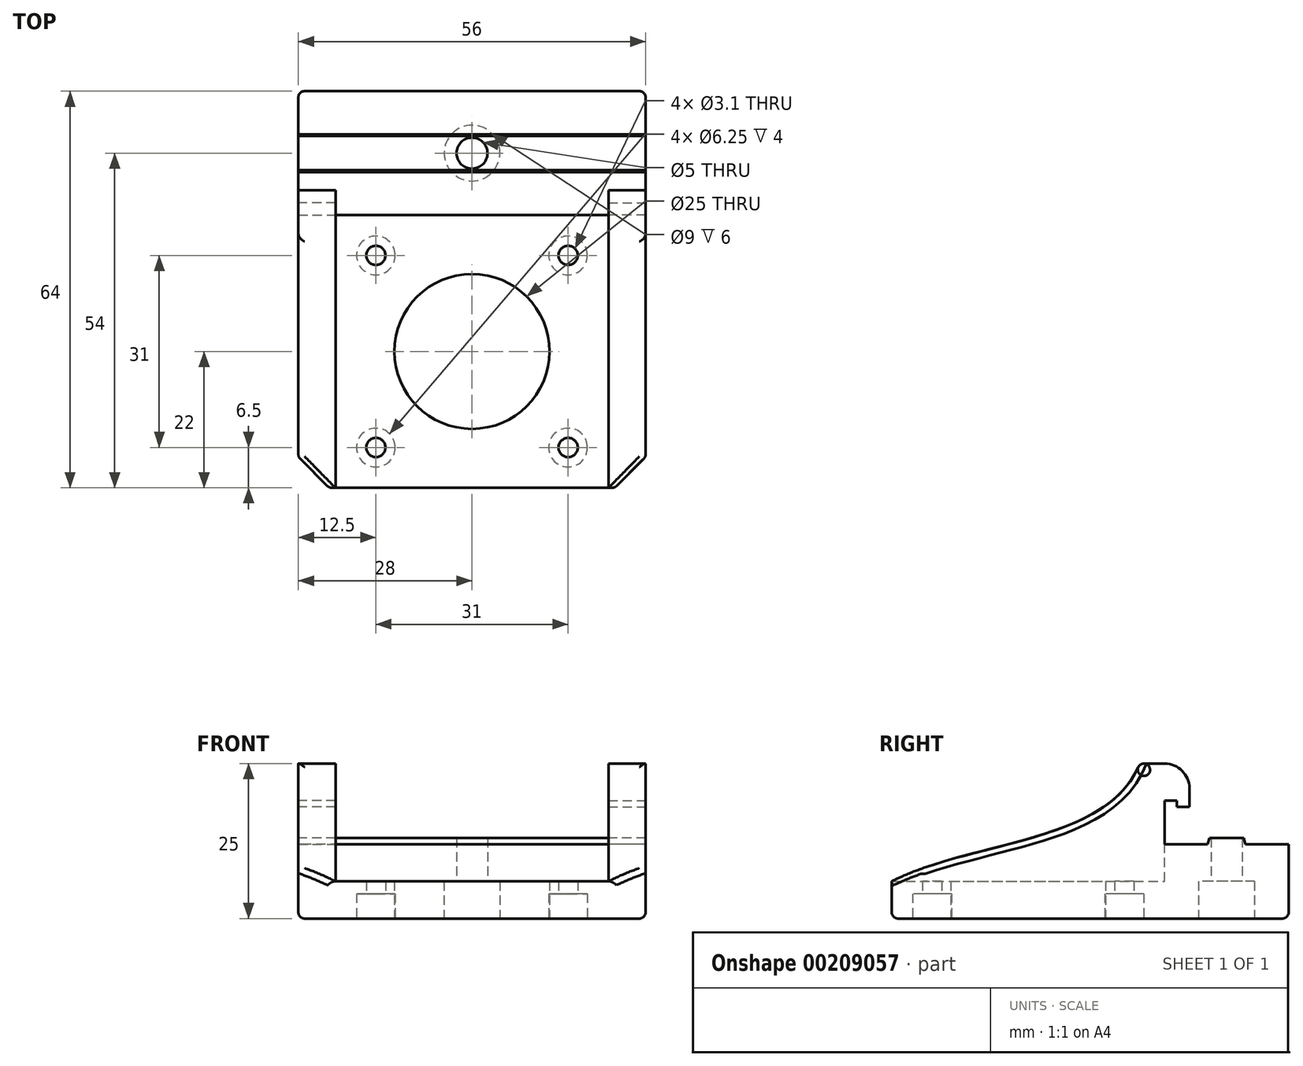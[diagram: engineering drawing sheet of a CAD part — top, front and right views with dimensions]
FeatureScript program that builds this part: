
annotation { "Feature Type Name" : "Feature", "Feature Type Description" : "" }
export const myFeature = defineFeature(function(context is Context, id is Id, definition is map)
    precondition{}
    {
        {
            var Q0;
            Q0=qCreatedBy(makeId("Right.planeOp"),FACE);
            var sketch = newSketch(context, id + "F0", { "sketchPlane" : qUnion([Q0])});
            skLineSegment(sketch, "E0", {"start": v(-6, 44) * mm, "end": v(0, 44) * mm});
            skLineSegment(sketch, "E1", {"start": v(0, 44) * mm, "end": v(0, 0) * mm});
            skLineSegment(sketch, "E2", {"start": v(0, 0) * mm, "end": v(6, 0) * mm});
            skLineSegment(sketch, "E3", {"start": v(6, 0) * mm, "end": v(6, -6.95) * mm});
            skLineSegment(sketch, "E4", {"start": v(7, -7.25) * mm, "end": v(7, -12.75) * mm});
            skLineSegment(sketch, "E5", {"start": v(7, -12.75) * mm, "end": v(6, -13.05) * mm});
            skLineSegment(sketch, "E6", {"start": v(6, -13.05) * mm, "end": v(6, -20) * mm});
            skLineSegment(sketch, "E7", {"start": v(6, -20) * mm, "end": v(-6, -20) * mm});
            skLineSegment(sketch, "E8", {"start": v(-6, -20) * mm, "end": v(-6, 44) * mm});
            skLineSegment(sketch, "E9", {"start": v(7, -7.25) * mm, "end": v(6, -6.95) * mm});
            skSolve(sketch);
        }
        {
            var Q0;
            Q0=makeQuery(id+"F0.imprint","IMPRINT",FACE,{"disambiguationData":[TD([[makeQuery(id+"F0.imprint","IMPRINT",EDGE,{"derivedFrom":sQuery(id+"F0.wireOp",EDGE,"E0")}),-1.0]])]});
            extrude(context, id + "F1", {"entities" : qUnion([Q0]), "endBound" : BoundingType.SYMMETRIC, "depth" : 56 * mm});
        }
        {
            var Q0;
            Q0=makeQuery(id+"F1.opExtrude","SWEPT_FACE",FACE,{"disambiguationData":[OSD([sQuery(id+"F0.wireOp",EDGE,"E8")])]});
            var sketch = newSketch(context, id + "F2", { "sketchPlane" : qUnion([Q0])});
            skLineSegment(sketch, "E10", {"start": v(-28, 44) * mm, "end": v(28, 0) * mm, "construction": true});
            skLineSegment(sketch, "E11", {"start": v(-28, 0) * mm, "end": v(28, 44) * mm, "construction": true});
            skLineSegment(sketch, "E12", {"start": v(-28, 0) * mm, "end": v(28, -20) * mm, "construction": true});
            skLineSegment(sketch, "E13", {"start": v(28, 0) * mm, "end": v(-28, -20) * mm, "construction": true});
            skLineSegment(sketch, "E14.bottom", {"start": v(-15.5, 37.5) * mm, "end": v(15.5, 37.5) * mm, "construction": true});
            skLineSegment(sketch, "E14.top", {"start": v(-15.5, 6.5) * mm, "end": v(15.5, 6.5) * mm, "construction": true});
            skLineSegment(sketch, "E14.left", {"start": v(-15.5, 37.5) * mm, "end": v(-15.5, 6.5) * mm, "construction": true});
            skLineSegment(sketch, "E14.right", {"start": v(15.5, 37.5) * mm, "end": v(15.5, 6.5) * mm, "construction": true});
            skLineSegment(sketch, "E15", {"start": v(-15.5, 37.5) * mm, "end": v(15.5, 6.5) * mm, "construction": true});
            skLineSegment(sketch, "E16", {"start": v(15.5, 37.5) * mm, "end": v(-15.5, 6.5) * mm, "construction": true});
            skPoint(sketch, "E17", {"position": v(0, 22) * mm});
            skCircle(sketch, "E18", {"center": v(-15.5, 37.5) * mm, "radius": 1.55 * mm});
            skCircle(sketch, "E19", {"center": v(15.5, 37.5) * mm, "radius": 1.55 * mm});
            skCircle(sketch, "E20", {"center": v(15.5, 6.5) * mm, "radius": 1.55 * mm});
            skCircle(sketch, "E21", {"center": v(-15.5, 6.5) * mm, "radius": 1.55 * mm});
            skPoint(sketch, "E22", {"position": v(0, -10) * mm});
            skCircle(sketch, "E23", {"center": v(0, -10) * mm, "radius": 2.5 * mm});
            skCircle(sketch, "E24", {"center": v(0, 22) * mm, "radius": 12.5 * mm});
            skCircle(sketch, "E25", {"center": v(0, -10) * mm, "radius": 4.5 * mm});
            skSolve(sketch);
        }
        {
            var Q0;
            Q0=makeQuery(id+"F2.imprint","IMPRINT",FACE,{"disambiguationData":[TD([[makeQuery(id+"F2.imprint","IMPRINT",EDGE,{"derivedFrom":sQuery(id+"F2.wireOp",EDGE,"E18")}),1.0]])]});
            var Q1;
            Q1=makeQuery(id+"F2.imprint","IMPRINT",FACE,{"disambiguationData":[TD([[makeQuery(id+"F2.imprint","IMPRINT",EDGE,{"derivedFrom":sQuery(id+"F2.wireOp",EDGE,"E19")}),1.0]])]});
            var Q2;
            Q2=makeQuery(id+"F2.imprint","IMPRINT",FACE,{"disambiguationData":[TD([[makeQuery(id+"F2.imprint","IMPRINT",EDGE,{"derivedFrom":sQuery(id+"F2.wireOp",EDGE,"E20")}),1.0]])]});
            var Q3;
            Q3=makeQuery(id+"F2.imprint","IMPRINT",FACE,{"disambiguationData":[TD([[makeQuery(id+"F2.imprint","IMPRINT",EDGE,{"derivedFrom":sQuery(id+"F2.wireOp",EDGE,"E21")}),1.0]])]});
            var Q4;
            Q4=makeQuery(id+"F2.imprint","IMPRINT",FACE,{"disambiguationData":[TD([[makeQuery(id+"F2.imprint","IMPRINT",EDGE,{"derivedFrom":sQuery(id+"F2.wireOp",EDGE,"E24")}),1.0]])]});
            var Q5;
            Q5=makeQuery(id+"F2.imprint","IMPRINT",FACE,{"disambiguationData":[TD([[makeQuery(id+"F2.imprint","IMPRINT",EDGE,{"derivedFrom":sQuery(id+"F2.wireOp",EDGE,"E23")}),1.0]])]});
            extrude(context, id + "F3", {"entities" : qUnion([Q0, Q1, Q2, Q3, Q4, Q5]), "operationType" : NewBodyOperationType.REMOVE, "endBound" : BoundingType.THROUGH_ALL, "oppositeDirection" : true, "depth" : 25 * mm});
        }
        {
            var Q0;
            Q0=makeQuery(id+"F2.imprint","IMPRINT",FACE,{"disambiguationData":[TD([[makeQuery(id+"F2.imprint","IMPRINT",EDGE,{"derivedFrom":sQuery(id+"F2.wireOp",EDGE,"E23")}),-1.0]])]});
            extrude(context, id + "F4", {"entities" : qUnion([Q0]), "operationType" : NewBodyOperationType.REMOVE, "oppositeDirection" : true, "depth" : 6 * mm});
        }
        {
            var Q0;
            Q0=makeQuery(id+"F1.opExtrude","CAP_FACE",FACE,{"disambiguationData":[OSD([sQuery(id+"F0.wireOp",EDGE,"E0"),sQuery(id+"F0.wireOp",EDGE,"E1"),sQuery(id+"F0.wireOp",EDGE,"E2"),sQuery(id+"F0.wireOp",EDGE,"E3"),sQuery(id+"F0.wireOp",EDGE,"E4"),sQuery(id+"F0.wireOp",EDGE,"E5"),sQuery(id+"F0.wireOp",EDGE,"E6"),sQuery(id+"F0.wireOp",EDGE,"E7"),sQuery(id+"F0.wireOp",EDGE,"E8"),sQuery(id+"F0.wireOp",EDGE,"E9")])],"isStart":false});
            var sketch = newSketch(context, id + "F5", { "sketchPlane" : qUnion([Q0])});
            skPoint(sketch, "E26.endSnap0", {"position": v(3, 0) * mm});
            skLineSegment(sketch, "E27", {"start": v(19, 4) * mm, "end": v(19, 4) * mm});
            skLineSegment(sketch, "E28", {"start": v(0, 44) * mm, "end": v(0, 0) * mm});
            skFitSpline(sketch, "E29", {"points": [v(0, 44) * mm, v(19, 4) * mm], "startDerivative": vector(20.02, -39.15) * mm, "endDerivative": vector(39, -15.68) * mm});
            skLineSegment(sketch, "E30", {"start": v(0, 0) * mm, "end": v(13, 0) * mm});
            skLineSegment(sketch, "E31", {"start": v(19, 0) * mm, "end": v(19, 4) * mm});
            skLineSegment(sketch, "E32", {"start": v(12, -4) * mm, "end": v(12, -2) * mm});
            skLineSegment(sketch, "E33", {"start": v(12, -2) * mm, "end": v(13, -2) * mm});
            skLineSegment(sketch, "E34", {"start": v(13, -2) * mm, "end": v(13, 0) * mm});
            skLineSegment(sketch, "E35", {"start": v(12, -4) * mm, "end": v(15, -4) * mm});
            skPoint(sketch, "E36.visualSharp", {"position": v(19, -4) * mm});
            skArc(sketch, "E36.filletArc", {"start": v(15, -4) * mm, "mid": v(17.83, -2.83) * mm, "end": v(19, 0) * mm});
            skSolve(sketch);
        }
        {
            var Q0;
            Q0=qSketchRegion(id+"F5",true);
            extrude(context, id + "F6", {"entities" : qUnion([Q0]), "operationType" : NewBodyOperationType.ADD, "oppositeDirection" : true, "depth" : 6 * mm});
        }
        {
            var Q0;
            Q0=makeQuery(id+"F1.opExtrude","SWEPT_BODY",BODY,{"disambiguationData":[OSD([sQuery(id+"F0.wireOp",EDGE,"E0"),sQuery(id+"F0.wireOp",EDGE,"E1"),sQuery(id+"F0.wireOp",EDGE,"E2"),sQuery(id+"F0.wireOp",EDGE,"E3"),sQuery(id+"F0.wireOp",EDGE,"E4"),sQuery(id+"F0.wireOp",EDGE,"E5"),sQuery(id+"F0.wireOp",EDGE,"E6"),sQuery(id+"F0.wireOp",EDGE,"E7"),sQuery(id+"F0.wireOp",EDGE,"E8"),sQuery(id+"F0.wireOp",EDGE,"E9")])]});
            var Q1;
            Q1=qCreatedBy(makeId("Right.planeOp"),FACE);
            mirror(context, id + "F7", {"operationType" : NewBodyOperationType.ADD, "entities" : qUnion([Q0]), "mirrorPlane" : qUnion([Q1])});
        }
        {
            var Q0;
            Q0=makeQuery(id+"F1.opExtrude","CAP_EDGE",EDGE,{"disambiguationData":[OSD([sQuery(id+"F0.wireOp",EDGE,"E0")])],"isStart":false});
            var Q1;
            Q1=makeQuery(id+"F1.opExtrude","CAP_EDGE",EDGE,{"disambiguationData":[OSD([sQuery(id+"F0.wireOp",EDGE,"E0")])],"isStart":true});
            chamfer(context, id + "F8", {"entities" : qUnion([Q0, Q1]), "width" : 5 * mm, "tangentPropagation" : true});
        }
        {
            var Q0;
            Q0=makeQuery(id+"F1.opExtrude","SWEPT_FACE",FACE,{"disambiguationData":[OSD([sQuery(id+"F0.wireOp",EDGE,"E8")])]});
            var sketch = newSketch(context, id + "F9", { "sketchPlane" : qUnion([Q0])});
            skCircle(sketch, "E37", {"center": v(-15.5, 37.5) * mm, "radius": 3.12 * mm});
            skCircle(sketch, "E38", {"center": v(15.5, 37.5) * mm, "radius": 3.12 * mm});
            skCircle(sketch, "E39", {"center": v(15.5, 6.5) * mm, "radius": 3.12 * mm});
            skCircle(sketch, "E40", {"center": v(-15.5, 6.5) * mm, "radius": 3.12 * mm});
            skSolve(sketch);
        }
        {
            var Q0;
            Q0=makeQuery(id+"F9.imprint","IMPRINT",FACE,{"disambiguationData":[TD([[makeQuery(id+"F9.imprint","IMPRINT",EDGE,{"derivedFrom":sQuery(id+"F9.wireOp",EDGE,"E37")}),1.0]])]});
            var Q1;
            Q1=makeQuery(id+"F9.imprint","IMPRINT",FACE,{"disambiguationData":[TD([[makeQuery(id+"F9.imprint","IMPRINT",EDGE,{"derivedFrom":sQuery(id+"F9.wireOp",EDGE,"E38")}),1.0]])]});
            var Q2;
            Q2=makeQuery(id+"F9.imprint","IMPRINT",FACE,{"disambiguationData":[TD([[makeQuery(id+"F9.imprint","IMPRINT",EDGE,{"derivedFrom":sQuery(id+"F9.wireOp",EDGE,"E39")}),1.0]])]});
            var Q3;
            Q3=makeQuery(id+"F9.imprint","IMPRINT",FACE,{"disambiguationData":[TD([[makeQuery(id+"F9.imprint","IMPRINT",EDGE,{"derivedFrom":sQuery(id+"F9.wireOp",EDGE,"E40")}),1.0]])]});
            extrude(context, id + "F10", {"entities" : qUnion([Q0, Q1, Q2, Q3]), "operationType" : NewBodyOperationType.REMOVE, "oppositeDirection" : true, "depth" : 4 * mm});
        }
        {
            var Q0;
            Q0=makeQuery(id+"F10.boolean.opBoolean","COPY",EDGE,{"derivedFrom":makeQuery(id+"F10.opExtrude","CAP_EDGE",EDGE,{"disambiguationData":[OSD([sQuery(id+"F9.wireOp",EDGE,"E37")])],"isStart":true})});
            var Q1;
            Q1=makeQuery(id+"F10.boolean.opBoolean","COPY",EDGE,{"derivedFrom":makeQuery(id+"F10.opExtrude","CAP_EDGE",EDGE,{"disambiguationData":[OSD([sQuery(id+"F9.wireOp",EDGE,"E38")])],"isStart":true})});
            var Q2;
            Q2=makeQuery(id+"F10.boolean.opBoolean","COPY",EDGE,{"derivedFrom":makeQuery(id+"F10.opExtrude","CAP_EDGE",EDGE,{"disambiguationData":[OSD([sQuery(id+"F9.wireOp",EDGE,"E40")])],"isStart":true})});
            var Q3;
            Q3=makeQuery(id+"F10.boolean.opBoolean","COPY",EDGE,{"derivedFrom":makeQuery(id+"F10.opExtrude","CAP_EDGE",EDGE,{"disambiguationData":[OSD([sQuery(id+"F9.wireOp",EDGE,"E39")])],"isStart":true})});
            var Q4;
            Q4=makeQuery(id+"F3.boolean.opBoolean","COPY",EDGE,{"derivedFrom":makeQuery(id+"F3.opExtrude","CAP_EDGE",EDGE,{"disambiguationData":[OSD([sQuery(id+"F2.wireOp",EDGE,"E24")])],"isStart":true})});
            var Q5;
            Q5=makeQuery(id+"F4.boolean.opBoolean","COPY",EDGE,{"derivedFrom":makeQuery(id+"F4.opExtrude","CAP_EDGE",EDGE,{"disambiguationData":[OSD([sQuery(id+"F2.wireOp",EDGE,"E25")])],"isStart":true})});
            var Q6;
            Q6=makeQuery(id+"F1.opExtrude","CAP_EDGE",EDGE,{"disambiguationData":[OSD([sQuery(id+"F0.wireOp",EDGE,"E8")])],"isStart":true});
            var Q7;
            Q7=makeQuery(id+"F1.opExtrude","SWEPT_EDGE",EDGE,{"disambiguationData":[OSD([sQuery(id+"F0.wireOp",EDGE,"E7"),sQuery(id+"F0.wireOp",EDGE,"E8")])]});
            var Q8;
            Q8=makeQuery(id+"F1.opExtrude","CAP_EDGE",EDGE,{"disambiguationData":[OSD([sQuery(id+"F0.wireOp",EDGE,"E8")])],"isStart":false});
            var Q9;
            Q9=makeQuery(id+"F8.opChamfer","BLEND_EDGE",EDGE,{"blendedFrom":[makeQuery(id+"F1.opExtrude","CAP_EDGE",EDGE,{"disambiguationData":[OSD([sQuery(id+"F0.wireOp",EDGE,"E0")])],"isStart":false}),makeQuery(id+"F1.opExtrude","SWEPT_FACE",FACE,{"disambiguationData":[OSD([sQuery(id+"F0.wireOp",EDGE,"E8")])]})],"blendedInto":[makeQuery(id+"F1.opExtrude","SWEPT_FACE",FACE,{"disambiguationData":[OSD([sQuery(id+"F0.wireOp",EDGE,"E8")])]})]});
            var Q10;
            Q10=makeQuery(id+"F1.opExtrude","SWEPT_EDGE",EDGE,{"disambiguationData":[OSD([sQuery(id+"F0.wireOp",EDGE,"E0"),sQuery(id+"F0.wireOp",EDGE,"E8")])]});
            var Q11;
            Q11=makeQuery(id+"F8.opChamfer","BLEND_EDGE",EDGE,{"blendedFrom":[makeQuery(id+"F1.opExtrude","CAP_EDGE",EDGE,{"disambiguationData":[OSD([sQuery(id+"F0.wireOp",EDGE,"E0")])],"isStart":true}),makeQuery(id+"F1.opExtrude","SWEPT_FACE",FACE,{"disambiguationData":[OSD([sQuery(id+"F0.wireOp",EDGE,"E8")])]})],"blendedInto":[makeQuery(id+"F1.opExtrude","SWEPT_FACE",FACE,{"disambiguationData":[OSD([sQuery(id+"F0.wireOp",EDGE,"E8")])]})]});
            var Q12;
            Q12=makeQuery(id+"F1.opExtrude","CAP_EDGE",EDGE,{"disambiguationData":[OSD([sQuery(id+"F0.wireOp",EDGE,"E7")])],"isStart":false});
            var Q13;
            Q13=makeQuery(id+"F1.opExtrude","CAP_EDGE",EDGE,{"disambiguationData":[OSD([sQuery(id+"F0.wireOp",EDGE,"E7")])],"isStart":true});
            var Q14;
            {var subQ0=sQuery(id+"F0.wireOp",EDGE,"E9");var subQ1=sQuery(id+"F0.wireOp",EDGE,"E8");var subQ2=sQuery(id+"F0.wireOp",EDGE,"E7");var subQ3=sQuery(id+"F0.wireOp",EDGE,"E6");var subQ4=sQuery(id+"F0.wireOp",EDGE,"E5");var subQ5=sQuery(id+"F0.wireOp",EDGE,"E4");var subQ6=sQuery(id+"F0.wireOp",EDGE,"E3");var subQ7=sQuery(id+"F0.wireOp",EDGE,"E2");var subQ8=sQuery(id+"F0.wireOp",EDGE,"E1");var subQ9=sQuery(id+"F0.wireOp",EDGE,"E0");Q14=makeQuery(id+"F8.opChamfer","BLEND_EDGE",EDGE,{"blendedFrom":[makeQuery(id+"F1.opExtrude","CAP_EDGE",EDGE,{"disambiguationData":[OSD([subQ9])],"isStart":true}),makeQuery(id+"F7.boolean.opBoolean","MERGE",FACE,{"derivedFrom":[makeQuery(id+"F1.opExtrude","CAP_FACE",FACE,{"disambiguationData":[OSD([subQ9,subQ8,subQ7,subQ6,subQ5,subQ4,subQ3,subQ2,subQ1,subQ0])],"isStart":true}),makeQuery(id+"F7.opPattern","COPY",FACE,{"derivedFrom":makeQuery(id+"F6.boolean.opBoolean","MERGE",FACE,{"derivedFrom":[makeQuery(id+"F1.opExtrude","CAP_FACE",FACE,{"disambiguationData":[OSD([subQ9,subQ8,subQ7,subQ6,subQ5,subQ4,subQ3,subQ2,subQ1,subQ0])],"isStart":false}),makeQuery(id+"F6.opExtrude","CAP_FACE",FACE,{"disambiguationData":[OSD([sQuery(id+"F5.wireOp",EDGE,"E26"),sQuery(id+"F5.wireOp",EDGE,"UbbL01kc-3hmS-gi7m-H064-AjZIugb0BuKS"),sQuery(id+"F5.wireOp",EDGE,"E27"),sQuery(id+"F5.wireOp",EDGE,"E28"),sQuery(id+"F5.wireOp",EDGE,"E29")])],"isStart":true})]}),"instanceName":"1"})]})],"blendedInto":[makeQuery(id+"F7.boolean.opBoolean","MERGE",FACE,{"derivedFrom":[makeQuery(id+"F1.opExtrude","CAP_FACE",FACE,{"disambiguationData":[OSD([subQ9,subQ8,subQ7,subQ6,subQ5,subQ4,subQ3,subQ2,subQ1,subQ0])],"isStart":true}),makeQuery(id+"F7.opPattern","COPY",FACE,{"derivedFrom":makeQuery(id+"F6.boolean.opBoolean","MERGE",FACE,{"derivedFrom":[makeQuery(id+"F1.opExtrude","CAP_FACE",FACE,{"disambiguationData":[OSD([subQ9,subQ8,subQ7,subQ6,subQ5,subQ4,subQ3,subQ2,subQ1,subQ0])],"isStart":false}),makeQuery(id+"F6.opExtrude","CAP_FACE",FACE,{"disambiguationData":[OSD([sQuery(id+"F5.wireOp",EDGE,"E26"),sQuery(id+"F5.wireOp",EDGE,"UbbL01kc-3hmS-gi7m-H064-AjZIugb0BuKS"),sQuery(id+"F5.wireOp",EDGE,"E27"),sQuery(id+"F5.wireOp",EDGE,"E28"),sQuery(id+"F5.wireOp",EDGE,"E29")])],"isStart":true})]}),"instanceName":"1"})]})]});}
            var Q15;
            {var subQ0=sQuery(id+"F0.wireOp",EDGE,"E0");Q15=makeQuery(id+"F8.opChamfer","BLEND_EDGE",EDGE,{"blendedFrom":[makeQuery(id+"F1.opExtrude","CAP_EDGE",EDGE,{"disambiguationData":[OSD([subQ0])],"isStart":false}),makeQuery(id+"F1.opExtrude","SWEPT_FACE",FACE,{"disambiguationData":[OSD([subQ0])]})],"blendedInto":[makeQuery(id+"F1.opExtrude","SWEPT_FACE",FACE,{"disambiguationData":[OSD([subQ0])]})]});}
            var Q16;
            {var subQ0=sQuery(id+"F0.wireOp",EDGE,"E0");Q16=makeQuery(id+"F8.opChamfer","BLEND_EDGE",EDGE,{"blendedFrom":[makeQuery(id+"F1.opExtrude","CAP_EDGE",EDGE,{"disambiguationData":[OSD([subQ0])],"isStart":true}),makeQuery(id+"F1.opExtrude","SWEPT_FACE",FACE,{"disambiguationData":[OSD([subQ0])]})],"blendedInto":[makeQuery(id+"F1.opExtrude","SWEPT_FACE",FACE,{"disambiguationData":[OSD([subQ0])]})]});}
            var Q17;
            {var subQ0=sQuery(id+"F0.wireOp",EDGE,"E0");Q17=makeQuery(id+"F8.opChamfer","BLEND_EDGE",EDGE,{"blendedFrom":[makeQuery(id+"F1.opExtrude","CAP_EDGE",EDGE,{"disambiguationData":[OSD([subQ0])],"isStart":false}),makeQuery(id+"F6.boolean.opBoolean","MERGE",FACE,{"derivedFrom":[makeQuery(id+"F1.opExtrude","CAP_FACE",FACE,{"disambiguationData":[OSD([subQ0,sQuery(id+"F0.wireOp",EDGE,"E1"),sQuery(id+"F0.wireOp",EDGE,"E2"),sQuery(id+"F0.wireOp",EDGE,"E3"),sQuery(id+"F0.wireOp",EDGE,"E4"),sQuery(id+"F0.wireOp",EDGE,"E5"),sQuery(id+"F0.wireOp",EDGE,"E6"),sQuery(id+"F0.wireOp",EDGE,"E7"),sQuery(id+"F0.wireOp",EDGE,"E8"),sQuery(id+"F0.wireOp",EDGE,"E9")])],"isStart":false}),makeQuery(id+"F6.opExtrude","CAP_FACE",FACE,{"disambiguationData":[OSD([sQuery(id+"F5.wireOp",EDGE,"E26"),sQuery(id+"F5.wireOp",EDGE,"UbbL01kc-3hmS-gi7m-H064-AjZIugb0BuKS"),sQuery(id+"F5.wireOp",EDGE,"E27"),sQuery(id+"F5.wireOp",EDGE,"E28"),sQuery(id+"F5.wireOp",EDGE,"E29")])],"isStart":true})]})],"blendedInto":[makeQuery(id+"F6.boolean.opBoolean","MERGE",FACE,{"derivedFrom":[makeQuery(id+"F1.opExtrude","CAP_FACE",FACE,{"disambiguationData":[OSD([subQ0,sQuery(id+"F0.wireOp",EDGE,"E1"),sQuery(id+"F0.wireOp",EDGE,"E2"),sQuery(id+"F0.wireOp",EDGE,"E3"),sQuery(id+"F0.wireOp",EDGE,"E4"),sQuery(id+"F0.wireOp",EDGE,"E5"),sQuery(id+"F0.wireOp",EDGE,"E6"),sQuery(id+"F0.wireOp",EDGE,"E7"),sQuery(id+"F0.wireOp",EDGE,"E8"),sQuery(id+"F0.wireOp",EDGE,"E9")])],"isStart":false}),makeQuery(id+"F6.opExtrude","CAP_FACE",FACE,{"disambiguationData":[OSD([sQuery(id+"F5.wireOp",EDGE,"E26"),sQuery(id+"F5.wireOp",EDGE,"UbbL01kc-3hmS-gi7m-H064-AjZIugb0BuKS"),sQuery(id+"F5.wireOp",EDGE,"E27"),sQuery(id+"F5.wireOp",EDGE,"E28"),sQuery(id+"F5.wireOp",EDGE,"E29")])],"isStart":true})]})]});}
            var Q18;
            {var subQ0=sQuery(id+"F5.wireOp",EDGE,"E29");var subQ1=sQuery(id+"F0.wireOp",EDGE,"E0");Q18=makeQuery(id+"FoMwGPE5wL7GN5E_1.boolean.opBoolean","SPLIT",EDGE,{"disambiguationData":[TD([makeQuery(id+"F1.opExtrude","SWEPT_FACE",FACE,{"disambiguationData":[OSD([subQ1])]})])],"derivedFrom":makeQuery(id+"F6.opExtrude","CAP_EDGE",EDGE,{"disambiguationData":[OSD([subQ0])],"isStart":true})});}
            var Q19;
            {var subQ0=sQuery(id+"F5.wireOp",EDGE,"E29");var subQ1=sQuery(id+"F0.wireOp",EDGE,"E0");Q19=makeQuery(id+"F7.opPattern","COPY",EDGE,{"derivedFrom":makeQuery(id+"FoMwGPE5wL7GN5E_1.boolean.opBoolean","SPLIT",EDGE,{"disambiguationData":[TD([makeQuery(id+"F1.opExtrude","SWEPT_FACE",FACE,{"disambiguationData":[OSD([subQ1])]})])],"derivedFrom":makeQuery(id+"F6.opExtrude","CAP_EDGE",EDGE,{"disambiguationData":[OSD([subQ0])],"isStart":true})}),"instanceName":"1"});}
            var Q20;
            {var subQ0=sQuery(id+"F5.wireOp",EDGE,"E29");var subQ1=sQuery(id+"F5.wireOp",EDGE,"E27");Q20=makeQuery(id+"F7.opPattern","COPY",EDGE,{"derivedFrom":makeQuery(id+"FoMwGPE5wL7GN5E_1.boolean.opBoolean","SPLIT",EDGE,{"disambiguationData":[TD([makeQuery(id+"F6.opExtrude","SWEPT_FACE",FACE,{"disambiguationData":[OSD([subQ1])]})])],"derivedFrom":makeQuery(id+"F6.opExtrude","CAP_EDGE",EDGE,{"disambiguationData":[OSD([subQ0])],"isStart":true})}),"instanceName":"1"});}
            var Q21;
            Q21=makeQuery(id+"F7.opPattern","COPY",EDGE,{"derivedFrom":makeQuery(id+"F6.opExtrude","CAP_EDGE",EDGE,{"disambiguationData":[OSD([sQuery(id+"F5.wireOp",EDGE,"E27")])],"isStart":true}),"instanceName":"1"});
            var Q22;
            Q22=makeQuery(id+"F7.opPattern","COPY",EDGE,{"derivedFrom":makeQuery(id+"F6.opExtrude","CAP_EDGE",EDGE,{"disambiguationData":[OSD([sQuery(id+"F5.wireOp",EDGE,"UbbL01kc-3hmS-gi7m-H064-AjZIugb0BuKS")])],"isStart":true}),"instanceName":"1"});
            var Q23;
            Q23=makeQuery(id+"F6.opExtrude","CAP_EDGE",EDGE,{"disambiguationData":[OSD([sQuery(id+"F5.wireOp",EDGE,"UbbL01kc-3hmS-gi7m-H064-AjZIugb0BuKS")])],"isStart":true});
            var Q24;
            Q24=makeQuery(id+"F6.opExtrude","CAP_EDGE",EDGE,{"disambiguationData":[OSD([sQuery(id+"F5.wireOp",EDGE,"E27")])],"isStart":true});
            var Q25;
            {var subQ0=sQuery(id+"F5.wireOp",EDGE,"E29");var subQ1=sQuery(id+"F5.wireOp",EDGE,"E27");Q25=makeQuery(id+"FoMwGPE5wL7GN5E_1.boolean.opBoolean","SPLIT",EDGE,{"disambiguationData":[TD([makeQuery(id+"F6.opExtrude","SWEPT_FACE",FACE,{"disambiguationData":[OSD([subQ1])]})])],"derivedFrom":makeQuery(id+"F6.opExtrude","CAP_EDGE",EDGE,{"disambiguationData":[OSD([subQ0])],"isStart":true})});}
            var Q26;
            Q26=makeQuery(id+"F7.opPattern","COPY",EDGE,{"derivedFrom":makeQuery(id+"F6.opExtrude","SWEPT_EDGE",EDGE,{"disambiguationData":[OSD([sQuery(id+"F5.wireOp",EDGE,"UbbL01kc-3hmS-gi7m-H064-AjZIugb0BuKS"),sQuery(id+"F5.wireOp",EDGE,"E27")])]}),"instanceName":"1"});
            var Q27;
            Q27=makeQuery(id+"F7.opPattern","COPY",EDGE,{"derivedFrom":makeQuery(id+"F6.opExtrude","SWEPT_EDGE",EDGE,{"disambiguationData":[OSD([sQuery(id+"F5.wireOp",EDGE,"E27"),sQuery(id+"F5.wireOp",EDGE,"E29")])]}),"instanceName":"1"});
            var Q28;
            Q28=makeQuery(id+"F6.opExtrude","SWEPT_EDGE",EDGE,{"disambiguationData":[OSD([sQuery(id+"F5.wireOp",EDGE,"E27"),sQuery(id+"F5.wireOp",EDGE,"E29")])]});
            var Q29;
            Q29=makeQuery(id+"FoMwGPE5wL7GN5E_1.boolean.opBoolean","INTERSECT",EDGE,{"disambiguationData":[OD(1.0)],"derivedFrom":[makeQuery(id+"F6.opExtrude","SWEPT_FACE",FACE,{"disambiguationData":[OSD([sQuery(id+"F5.wireOp",EDGE,"E29")])]}),makeQuery(id+"FoMwGPE5wL7GN5E_1.opExtrude","SWEPT_FACE",FACE,{"disambiguationData":[OSD([sQuery(id+"FBNlypT3mVyOmz6_1.wireOp",EDGE,"qYlRFCWZ-tTDc-EFRd-Qzht-gGidoPvth087")])]})]});
            var Q30;
            Q30=makeQuery(id+"F7.opPattern","COPY",EDGE,{"derivedFrom":makeQuery(id+"FoMwGPE5wL7GN5E_1.boolean.opBoolean","INTERSECT",EDGE,{"disambiguationData":[OD(1.0)],"derivedFrom":[makeQuery(id+"F6.opExtrude","SWEPT_FACE",FACE,{"disambiguationData":[OSD([sQuery(id+"F5.wireOp",EDGE,"E29")])]}),makeQuery(id+"FoMwGPE5wL7GN5E_1.opExtrude","SWEPT_FACE",FACE,{"disambiguationData":[OSD([sQuery(id+"FBNlypT3mVyOmz6_1.wireOp",EDGE,"qYlRFCWZ-tTDc-EFRd-Qzht-gGidoPvth087")])]})]}),"instanceName":"1"});
            var Q31;
            Q31=makeQuery(id+"F7.opPattern","COPY",EDGE,{"derivedFrom":makeQuery(id+"FoMwGPE5wL7GN5E_1.boolean.opBoolean","INTERSECT",EDGE,{"disambiguationData":[OD(0.0)],"derivedFrom":[makeQuery(id+"F6.opExtrude","SWEPT_FACE",FACE,{"disambiguationData":[OSD([sQuery(id+"F5.wireOp",EDGE,"E29")])]}),makeQuery(id+"FoMwGPE5wL7GN5E_1.opExtrude","SWEPT_FACE",FACE,{"disambiguationData":[OSD([sQuery(id+"FBNlypT3mVyOmz6_1.wireOp",EDGE,"qYlRFCWZ-tTDc-EFRd-Qzht-gGidoPvth087")])]})]}),"instanceName":"1"});
            var Q32;
            Q32=makeQuery(id+"FoMwGPE5wL7GN5E_1.boolean.opBoolean","INTERSECT",EDGE,{"disambiguationData":[OD(0.0)],"derivedFrom":[makeQuery(id+"F6.opExtrude","SWEPT_FACE",FACE,{"disambiguationData":[OSD([sQuery(id+"F5.wireOp",EDGE,"E29")])]}),makeQuery(id+"FoMwGPE5wL7GN5E_1.opExtrude","SWEPT_FACE",FACE,{"disambiguationData":[OSD([sQuery(id+"FBNlypT3mVyOmz6_1.wireOp",EDGE,"qYlRFCWZ-tTDc-EFRd-Qzht-gGidoPvth087")])]})]});
            var Q33;
            {var subQ0=sQuery(id+"F5.wireOp",EDGE,"E29");var subQ6=sQuery(id+"F0.wireOp",EDGE,"E0");Q33=makeQuery(id+"F8.opChamfer","BLEND_EDGE",EDGE,{"blendedFrom":[makeQuery(id+"F1.opExtrude","CAP_EDGE",EDGE,{"disambiguationData":[OSD([subQ6])],"isStart":false}),makeQuery(id+"FoMwGPE5wL7GN5E_1.boolean.opBoolean","SPLIT",FACE,{"disambiguationData":[TD([makeQuery(id+"F1.opExtrude","SWEPT_FACE",FACE,{"disambiguationData":[OSD([subQ6])]})])],"derivedFrom":makeQuery(id+"F6.opExtrude","SWEPT_FACE",FACE,{"disambiguationData":[OSD([subQ0])]})})],"blendedInto":[makeQuery(id+"FoMwGPE5wL7GN5E_1.boolean.opBoolean","SPLIT",FACE,{"disambiguationData":[TD([makeQuery(id+"F1.opExtrude","SWEPT_FACE",FACE,{"disambiguationData":[OSD([subQ6])]})])],"derivedFrom":makeQuery(id+"F6.opExtrude","SWEPT_FACE",FACE,{"disambiguationData":[OSD([subQ0])]})})]});}
            var Q34;
            {var subQ0=sQuery(id+"F5.wireOp",EDGE,"E29");var subQ6=sQuery(id+"F0.wireOp",EDGE,"E0");Q34=makeQuery(id+"F8.opChamfer","BLEND_EDGE",EDGE,{"blendedFrom":[makeQuery(id+"F1.opExtrude","CAP_EDGE",EDGE,{"disambiguationData":[OSD([subQ6])],"isStart":true}),makeQuery(id+"F7.opPattern","COPY",FACE,{"derivedFrom":makeQuery(id+"FoMwGPE5wL7GN5E_1.boolean.opBoolean","SPLIT",FACE,{"disambiguationData":[TD([makeQuery(id+"F1.opExtrude","SWEPT_FACE",FACE,{"disambiguationData":[OSD([subQ6])]})])],"derivedFrom":makeQuery(id+"F6.opExtrude","SWEPT_FACE",FACE,{"disambiguationData":[OSD([subQ0])]})}),"instanceName":"1"})],"blendedInto":[makeQuery(id+"F7.opPattern","COPY",FACE,{"derivedFrom":makeQuery(id+"FoMwGPE5wL7GN5E_1.boolean.opBoolean","SPLIT",FACE,{"disambiguationData":[TD([makeQuery(id+"F1.opExtrude","SWEPT_FACE",FACE,{"disambiguationData":[OSD([subQ6])]})])],"derivedFrom":makeQuery(id+"F6.opExtrude","SWEPT_FACE",FACE,{"disambiguationData":[OSD([subQ0])]})}),"instanceName":"1"})]});}
            var Q35;
            Q35=makeQuery(id+"F6.opExtrude","SWEPT_EDGE",EDGE,{"disambiguationData":[OSD([sQuery(id+"F5.wireOp",EDGE,"UbbL01kc-3hmS-gi7m-H064-AjZIugb0BuKS"),sQuery(id+"F5.wireOp",EDGE,"E27")])]});
            fillet(context, id + "F11", {"entities" : qUnion([Q0, Q1, Q2, Q3, Q4, Q5, Q6, Q7, Q8, Q9, Q10, Q11, Q12, Q13, Q14, Q15, Q16, Q17, Q18, Q19, Q20, Q21, Q22, Q23, Q24, Q25, Q26, Q27, Q28, Q29, Q30, Q31, Q32, Q33, Q34, Q35]), "radius" : 1 * mm, "tangentPropagation" : true, "allowEdgeOverflow" : false});
        }
        {
            var Q0;
            Q0=makeQuery(id+"F1.opExtrude","SWEPT_BODY",BODY,{"disambiguationData":[OSD([sQuery(id+"F0.wireOp",EDGE,"E0"),sQuery(id+"F0.wireOp",EDGE,"E1"),sQuery(id+"F0.wireOp",EDGE,"E2"),sQuery(id+"F0.wireOp",EDGE,"E3"),sQuery(id+"F0.wireOp",EDGE,"E4"),sQuery(id+"F0.wireOp",EDGE,"E5"),sQuery(id+"F0.wireOp",EDGE,"E6"),sQuery(id+"F0.wireOp",EDGE,"E7"),sQuery(id+"F0.wireOp",EDGE,"E8"),sQuery(id+"F0.wireOp",EDGE,"E9")])]});
            var Q1;
            {var subQ1=sQuery(id+"F0.wireOp",EDGE,"E3");var subQ2=sQuery(id+"F0.wireOp",EDGE,"E2");Q1=makeQuery(id+"F7.boolean.opBoolean","SPLIT",EDGE,{"derivedFrom":makeQuery(id+"F6.boolean.opBoolean","SPLIT",EDGE,{"disambiguationData":[TD([makeQuery(id+"F1.opExtrude","CAP_FACE",FACE,{"disambiguationData":[OSD([sQuery(id+"F0.wireOp",EDGE,"E0"),sQuery(id+"F0.wireOp",EDGE,"E1"),subQ2,subQ1,sQuery(id+"F0.wireOp",EDGE,"E4"),sQuery(id+"F0.wireOp",EDGE,"E5"),sQuery(id+"F0.wireOp",EDGE,"E6"),sQuery(id+"F0.wireOp",EDGE,"E7"),sQuery(id+"F0.wireOp",EDGE,"E8"),sQuery(id+"F0.wireOp",EDGE,"E9")])],"isStart":true})])],"derivedFrom":makeQuery(id+"F1.opExtrude","SWEPT_EDGE",EDGE,{"disambiguationData":[OSD([subQ2,subQ1])]})})});}
            transform(context, id + "F12", {"entities" : qUnion([Q0]), "transformType" : TransformType.ROTATION, "transformAxis" : qUnion([Q1]), "angle" : 90 * degree, "oppositeDirection" : true, "makeCopy" : false});
        }
    });
